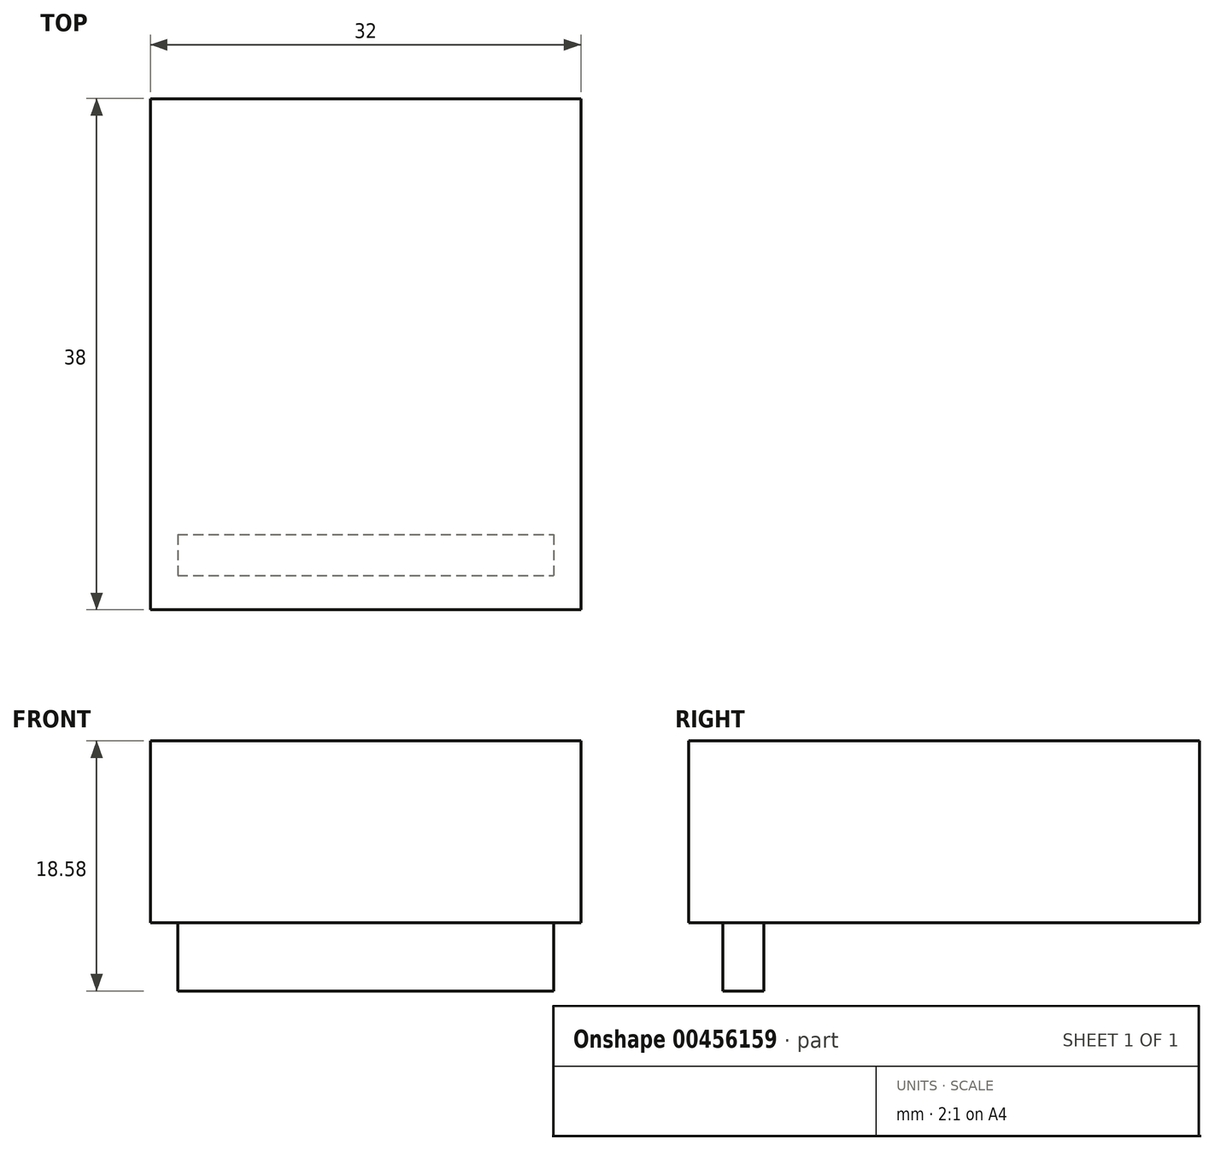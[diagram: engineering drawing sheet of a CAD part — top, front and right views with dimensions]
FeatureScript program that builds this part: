
annotation { "Feature Type Name" : "Feature", "Feature Type Description" : "" }
export const myFeature = defineFeature(function(context is Context, id is Id, definition is map)
    precondition{}
    {
        {
            var Q0;
            Q0=qCreatedBy(makeId("Top.planeOp"),FACE);
            var sketch = newSketch(context, id + "F0", { "sketchPlane" : qUnion([Q0])});
            skLineSegment(sketch, "E0.bottom", {"start": v(-13.97, 1.52) * mm, "end": v(13.97, 1.52) * mm});
            skLineSegment(sketch, "E0.top", {"start": v(-13.97, -1.52) * mm, "end": v(13.97, -1.52) * mm});
            skLineSegment(sketch, "E0.left", {"start": v(-13.97, 1.52) * mm, "end": v(-13.97, -1.52) * mm});
            skLineSegment(sketch, "E0.right", {"start": v(13.97, 1.52) * mm, "end": v(13.97, -1.52) * mm});
            skPoint(sketch, "E1", {"position": v(0, 0) * mm});
            skSolve(sketch);
        }
        {
            var Q0;
            Q0 = qSketchRegion(id + "F0", true);
            extrude(context, id + "F1", {"entities" : qUnion([Q0]), "depth" : 5.08 * mm});
        }
        {
            var Q0;
            Q0=makeQuery(id+"F1.opExtrude","CAP_FACE",FACE,{"disambiguationData":[OSD([sQuery(id+"F0.wireOp",EDGE,"E0.bottom"),sQuery(id+"F0.wireOp",EDGE,"E0.top"),sQuery(id+"F0.wireOp",EDGE,"E0.left"),sQuery(id+"F0.wireOp",EDGE,"E0.right")])],"isStart":false});
            var sketch = newSketch(context, id + "F2", { "sketchPlane" : qUnion([Q0])});
            skLineSegment(sketch, "E2.bottom", {"start": v(16, 33.94) * mm, "end": v(-16, 33.94) * mm});
            skLineSegment(sketch, "E2.top", {"start": v(16, -4.06) * mm, "end": v(-16, -4.06) * mm});
            skLineSegment(sketch, "E2.left", {"start": v(16, 33.94) * mm, "end": v(16, -4.06) * mm});
            skLineSegment(sketch, "E2.right", {"start": v(-16, 33.94) * mm, "end": v(-16, -4.06) * mm});
            skPoint(sketch, "E2.middle", {"position": v(0, 14.94) * mm});
            skPoint(sketch, "E3", {"position": v(0, -4.06) * mm});
            skSolve(sketch);
        }
        {
            var Q0;
            Q0=makeQuery(id+"F2.imprint","IMPRINT",FACE,{"disambiguationData":[TD([[makeQuery(id+"F2.imprint","IMPRINT",EDGE,{"derivedFrom":sQuery(id+"F2.wireOp",EDGE,"E2.bottom")}),1.0]])]});
            var Q1;
            Q1=makeQuery(id+"F2.imprint","IMPRINT",FACE,{"disambiguationData":[TD([[makeQuery(id+"F2.imprint","IMPRINT",EDGE,{"derivedFrom":makeQuery(id+"F1.opExtrude","CAP_EDGE",EDGE,{"disambiguationData":[OSD([sQuery(id+"F0.wireOp",EDGE,"E0.bottom")])],"isStart":false})}),-1.0]])]});
            extrude(context, id + "F3", {"entities" : qUnion([Q0, Q1]), "operationType" : NewBodyOperationType.ADD, "depth" : 13.5 * mm});
        }
    });
